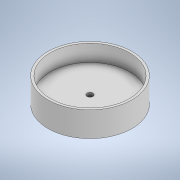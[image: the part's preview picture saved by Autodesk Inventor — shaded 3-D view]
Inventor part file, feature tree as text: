
AUTODESK INVENTOR PART (.ipt)
format: ipt  version: 2020 (Build 240168000, 168)  size: 117,248 bytes
history: native  units: mm
features: sketch x3, extrude x2, hole x1
ambient origin geometry x8: Origin, YZ Plane, XZ Plane, XY Plane, X Axis, Y Axis, Z Axis, Center Point
bodies: Solid1 (feature_tree)
feature tree (6):
  extrude  "Extrusion1"  Depth=9.0mm TaperAngle=0.0deg
  extrude  "Extrusion2"  Depth=18.0mm TaperAngle=0.0deg
  hole  "Hole1"  [1 undecoded]
  sketch  "Sketch1"  dims[d0=91.0mm d1=9.0mm d2=0.0mm]
  sketch  "Sketch2"  dims[d3=2.5mm d4=18.0mm d5=0.0mm]
  sketch  "Sketch3"  dims[d6=5.9mm d7=6.0mm d8=6.5mm d9=2.0mm d10=90.0deg d11=8.5mm d12=0.0mm]
note: 1 required parameter value undecoded (feature->parameter linkage not recoverable at this tier; creation-order binding heuristic only, values carry confidence <= 0.55)
